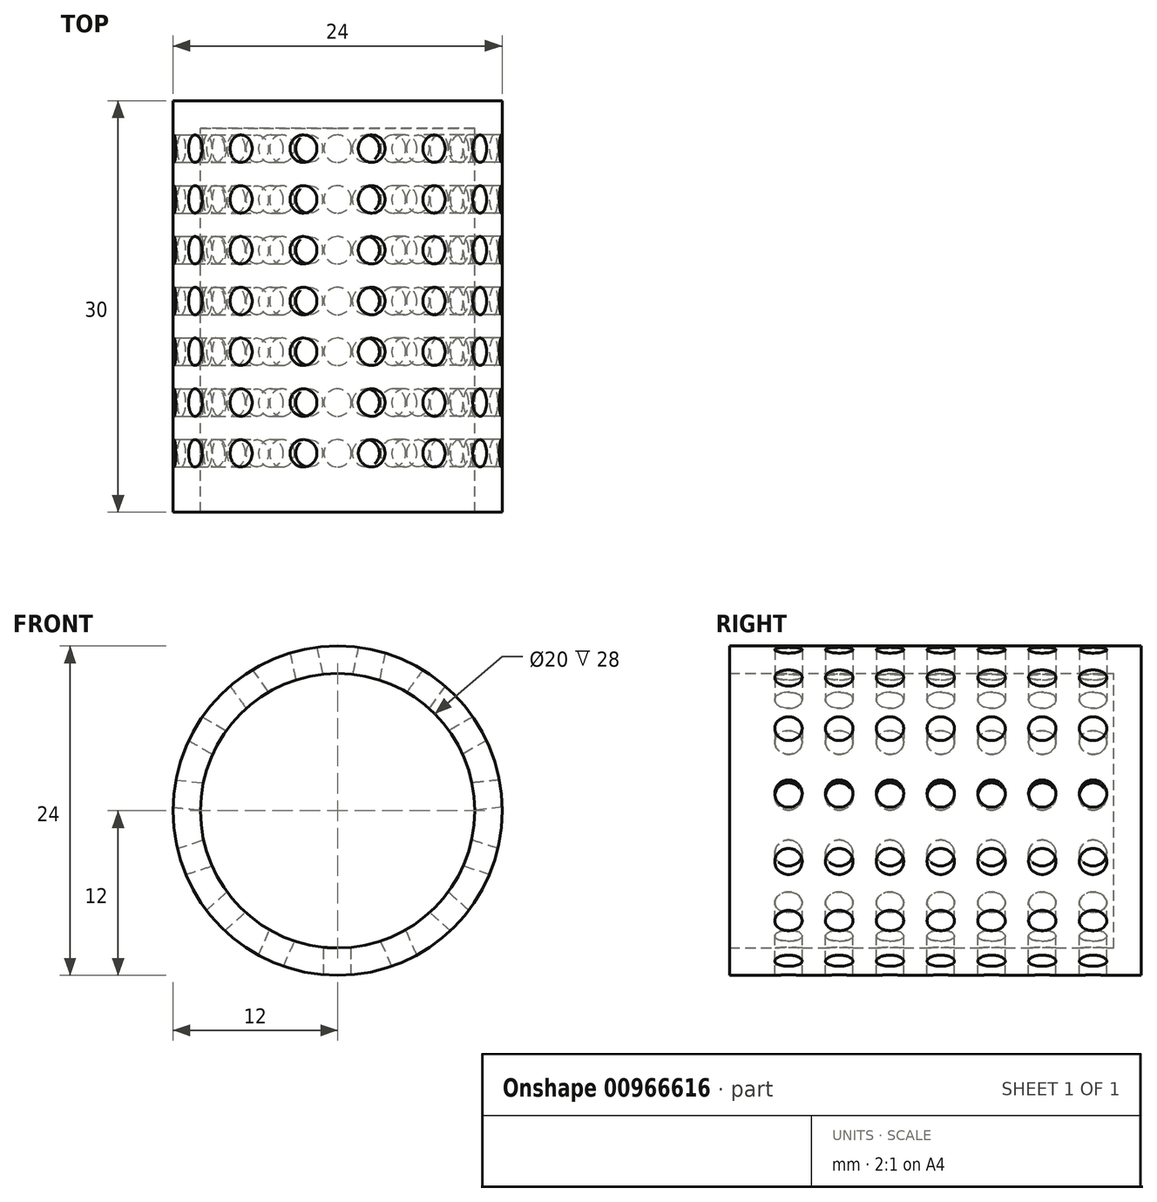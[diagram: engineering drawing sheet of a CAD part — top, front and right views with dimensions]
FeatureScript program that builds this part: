
annotation { "Feature Type Name" : "Feature", "Feature Type Description" : "" }
export const myFeature = defineFeature(function(context is Context, id is Id, definition is map)
    precondition{}
    {
        {
            var Q0;
            Q0=qCreatedBy(makeId("Front.planeOp"),FACE);
            var sketch = newSketch(context, id + "F0", { "sketchPlane" : qUnion([Q0])});
            skCircle(sketch, "E0", {"center": v(0, 0) * mm, "radius": 12 * mm});
            skSolve(sketch);
        }
        {
            var Q0;
            Q0 = qSketchRegion(id + "F0", true);
            extrude(context, id + "F1", {"entities" : qUnion([Q0]), "depth" : 30 * mm, "offsetDistance" : 25 * mm});
        }
        {
            var Q0;
            Q0=makeQuery(id+"F1.opExtrude","CAP_FACE",FACE,{"disambiguationData":[OSD([sQuery(id+"F0.wireOp",EDGE,"E0")])],"isStart":false});
            shell(context, id + "F2", {"entities" : qUnion([Q0]), "thickness" : 2 * mm});
        }
        {
            var Q0;
            Q0=qCreatedBy(makeId("Top.planeOp"),FACE);
            var sketch = newSketch(context, id + "F3", { "sketchPlane" : qUnion([Q0])});
            skCircle(sketch, "E1", {"center": v(0, -3.5) * mm, "radius": 1 * mm});
            skCircle(sketch, "E2.0.1.0", {"center": v(0, -7.2) * mm, "radius": 1 * mm});
            skCircle(sketch, "E2.0.2.0", {"center": v(0, -10.9) * mm, "radius": 1 * mm});
            skCircle(sketch, "E2.0.3.0", {"center": v(0, -14.6) * mm, "radius": 1 * mm});
            skCircle(sketch, "E2.0.4.0", {"center": v(0, -18.3) * mm, "radius": 1 * mm});
            skCircle(sketch, "E2.0.5.0", {"center": v(0, -22) * mm, "radius": 1 * mm});
            skCircle(sketch, "E2.0.6.0", {"center": v(0, -25.7) * mm, "radius": 1 * mm});
            skLineSegment(sketch, "E2.direction1", {"start": v(0, -3.5) * mm, "end": v(25, -3.5) * mm, "construction": true});
            skLineSegment(sketch, "E2.direction2", {"start": v(0, -3.5) * mm, "end": v(0, -7.2) * mm, "construction": true});
            skSolve(sketch);
        }
        {
            var Q0;
            Q0 = qSketchRegion(id + "F3", true);
            extrude(context, id + "F4", {"entities" : qUnion([Q0]), "operationType" : NewBodyOperationType.REMOVE, "oppositeDirection" : true, "depth" : 25 * mm, "offsetDistance" : 25 * mm});
        }
        {
            var Q0;
            Q0=makeQuery(id+"F4.boolean.opBoolean","COPY",FACE,{"derivedFrom":makeQuery(id+"F4.opExtrude","SWEPT_FACE",FACE,{"disambiguationData":[OSD([sQuery(id+"F3.wireOp",EDGE,"E1")])]})});
            var Q1;
            Q1=makeQuery(id+"F4.boolean.opBoolean","COPY",FACE,{"derivedFrom":makeQuery(id+"F4.opExtrude","SWEPT_FACE",FACE,{"disambiguationData":[OSD([sQuery(id+"F3.wireOp",EDGE,"E2.0.1.0")])]})});
            var Q2;
            Q2=makeQuery(id+"F4.boolean.opBoolean","COPY",FACE,{"derivedFrom":makeQuery(id+"F4.opExtrude","SWEPT_FACE",FACE,{"disambiguationData":[OSD([sQuery(id+"F3.wireOp",EDGE,"E2.0.2.0")])]})});
            var Q3;
            Q3=makeQuery(id+"F4.boolean.opBoolean","COPY",FACE,{"derivedFrom":makeQuery(id+"F4.opExtrude","SWEPT_FACE",FACE,{"disambiguationData":[OSD([sQuery(id+"F3.wireOp",EDGE,"E2.0.3.0")])]})});
            var Q4;
            Q4=makeQuery(id+"F4.boolean.opBoolean","COPY",FACE,{"derivedFrom":makeQuery(id+"F4.opExtrude","SWEPT_FACE",FACE,{"disambiguationData":[OSD([sQuery(id+"F3.wireOp",EDGE,"E2.0.4.0")])]})});
            var Q5;
            Q5=makeQuery(id+"F4.boolean.opBoolean","COPY",FACE,{"derivedFrom":makeQuery(id+"F4.opExtrude","SWEPT_FACE",FACE,{"disambiguationData":[OSD([sQuery(id+"F3.wireOp",EDGE,"E2.0.5.0")])]})});
            var Q6;
            Q6=makeQuery(id+"F4.boolean.opBoolean","COPY",FACE,{"derivedFrom":makeQuery(id+"F4.opExtrude","SWEPT_FACE",FACE,{"disambiguationData":[OSD([sQuery(id+"F3.wireOp",EDGE,"E2.0.6.0")])]})});
            var Q7;
            Q7=makeQuery(id+"F1.opExtrude","SWEPT_FACE",FACE,{"disambiguationData":[OSD([sQuery(id+"F0.wireOp",EDGE,"E0")])]});
            circularPattern(context, id + "F5", {"patternType" : PatternType.FACE, "operationType" : NewBodyOperationType.REMOVE, "faces" : qUnion([Q0, Q1, Q2, Q3, Q4, Q5, Q6]), "axis" : qUnion([Q7]), "angle" : 360 * degree, "instanceCount" : 15, "equalSpace" : true});
        }
    });
